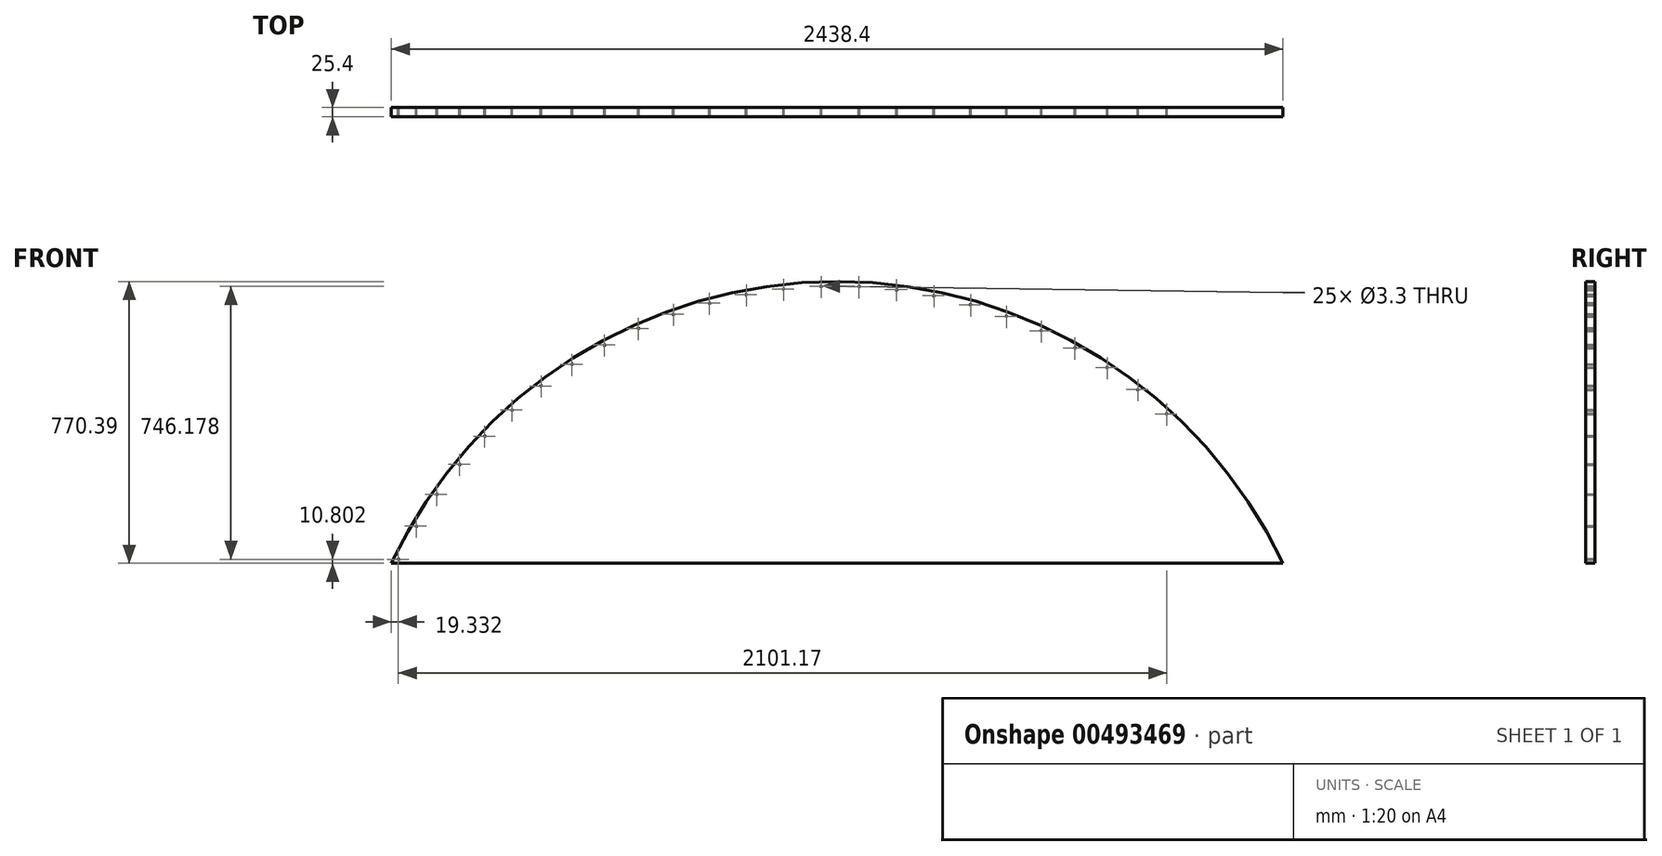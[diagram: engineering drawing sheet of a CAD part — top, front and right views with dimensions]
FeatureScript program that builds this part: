
annotation { "Feature Type Name" : "Feature", "Feature Type Description" : "" }
export const myFeature = defineFeature(function(context is Context, id is Id, definition is map)
    precondition{}
    {
        {
            var Q0;
            Q0=qCreatedBy(makeId("Front.planeOp"),FACE);
            var sketch = newSketch(context, id + "F0", { "sketchPlane" : qUnion([Q0])});
            skArc(sketch, "E0", {"start": v(1219.2, 0) * mm, "mid": v(0, 770.39) * mm, "end": v(-1219.2, 0) * mm});
            skLineSegment(sketch, "E1", {"start": v(-1219.2, 0) * mm, "end": v(1219.2, 0) * mm});
            skLineSegment(sketch, "E2", {"start": v(0, -579.55) * mm, "end": v(-923.4, 883.94) * mm, "construction": true});
            skLineSegment(sketch, "E3", {"start": v(0, -579.55) * mm, "end": v(0, 1034.52) * mm, "construction": true});
            skLineSegment(sketch, "E4", {"start": v(0, -579.55) * mm, "end": v(860.18, 783.76) * mm, "construction": true});
            skLineSegment(sketch, "E5", {"start": v(0, -579.55) * mm, "end": v(-1219.2, 0) * mm, "construction": true});
            skLineSegment(sketch, "E6", {"start": v(0, -579.55) * mm, "end": v(1219.2, 0) * mm, "construction": true});
            skArc(sketch, "E7.0", {"start": v(1196.26, -10.9) * mm, "mid": v(0, 744.99) * mm, "end": v(-1196.26, -10.9) * mm});
            skArc(sketch, "E8.0", {"start": v(1207.73, -5.45) * mm, "mid": v(0, 757.69) * mm, "end": v(-1207.73, -5.45) * mm, "construction": true});
            skPoint(sketch, "E9", {"position": v(-1199.87, 10.8) * mm});
            skPoint(sketch, "E10.1.0", {"position": v(-1150.75, 101.6) * mm});
            skPoint(sketch, "E10.2.0", {"position": v(-1094.78, 188.34) * mm});
            skPoint(sketch, "E10.3.0", {"position": v(-1032.29, 270.5) * mm});
            skPoint(sketch, "E10.4.0", {"position": v(-963.64, 347.6) * mm});
            skPoint(sketch, "E10.5.0", {"position": v(-889.25, 419.17) * mm});
            skPoint(sketch, "E10.6.0", {"position": v(-809.56, 484.79) * mm});
            skPoint(sketch, "E10.7.0", {"position": v(-725.05, 544.07) * mm});
            skPoint(sketch, "E10.8.0", {"position": v(-636.21, 596.65) * mm});
            skPoint(sketch, "E10.9.0", {"position": v(-543.58, 642.22) * mm});
            skPoint(sketch, "E10.10.0", {"position": v(-447.72, 680.51) * mm});
            skPoint(sketch, "E10.11.0", {"position": v(-349.19, 711.3) * mm});
            skPoint(sketch, "E10.12.0", {"position": v(-248.57, 734.38) * mm});
            skPoint(sketch, "E10.13.0", {"position": v(-146.47, 749.64) * mm});
            skPoint(sketch, "E10.14.0", {"position": v(-43.5, 756.98) * mm});
            skPoint(sketch, "E10.15.0", {"position": v(59.72, 756.35) * mm});
            skPoint(sketch, "E10.16.0", {"position": v(162.6, 747.77) * mm});
            skPoint(sketch, "E10.17.0", {"position": v(264.5, 731.27) * mm});
            skPoint(sketch, "E10.18.0", {"position": v(364.82, 706.96) * mm});
            skPoint(sketch, "E10.19.0", {"position": v(462.98, 674.99) * mm});
            skPoint(sketch, "E10.20.0", {"position": v(558.37, 635.53) * mm});
            skPoint(sketch, "E10.21.0", {"position": v(650.44, 588.84) * mm});
            skPoint(sketch, "E10.22.0", {"position": v(738.63, 535.19) * mm});
            skPoint(sketch, "E10.23.0", {"position": v(822.42, 474.89) * mm});
            skPoint(sketch, "E10.24.0", {"position": v(901.3, 408.3) * mm});
            skPoint(sketch, "E10.25.0", {"position": v(974.82, 335.84) * mm});
            skPoint(sketch, "E10.26.0", {"position": v(1042.53, 257.91) * mm});
            skPoint(sketch, "E10.27.0", {"position": v(1104.02, 175) * mm});
            skPoint(sketch, "E10.28.0", {"position": v(1158.94, 87.59) * mm});
            skPoint(sketch, "E10.29.0", {"position": v(1206.94, -3.8) * mm});
            skLineSegment(sketch, "E10.anchor1", {"start": v(0, -579.55) * mm, "end": v(-1199.87, 10.8) * mm, "construction": true});
            skLineSegment(sketch, "E10.anchor2", {"start": v(0, -579.55) * mm, "end": v(1206.94, -3.8) * mm, "construction": true});
            skSolve(sketch);
        }
        {
            var Q0;
            Q0 = qSketchRegion(id + "F0", true);
            extrude(context, id + "F1", {"entities" : qUnion([Q0]), "oppositeDirection" : true, "depth" : 25.4 * mm, "offsetDistance" : 25.4 * mm});
        }
        {
            var Q0;
            Q0=makeQuery(id+"F0.imprint","IMPRINT",FACE,{"disambiguationData":[TD([[makeQuery(id+"F0.imprint","IMPRINT",EDGE,{"derivedFrom":sQuery(id+"F0.wireOp",EDGE,"E0")}),1.0]])]});
            var sketch = newSketch(context, id + "F2", { "sketchPlane" : qUnion([Q0])});
            skLineSegment(sketch, "E11", {"start": v(-1385.99, 67.82) * mm, "end": v(1291.38, 67.82) * mm, "construction": true});
            skLineSegment(sketch, "E12.0", {"start": v(-1219.2, 0) * mm, "end": v(1219.2, 0) * mm});
            skSolve(sketch);
        }
        {
            var Q0;
            Q0=makeQuery(id+"F0.imprint","IMPRINT",FACE,{"disambiguationData":[TD([[makeQuery(id+"F0.imprint","IMPRINT",EDGE,{"derivedFrom":sQuery(id+"F0.wireOp",EDGE,"E0")}),1.0]])]});
            cPlane(context, id + "F3", {"entities" : qUnion([Q0]), "cplaneType" : CPlaneType.OFFSET, "offset" : 160.02 * mm, "width" : 152.4 * mm, "height" : 152.4 * mm});
        }
        {
            var Q0;
            Q0=qCreatedBy(id+"F3.planeOp",FACE);
            var sketch = newSketch(context, id + "F4", { "sketchPlane" : qUnion([Q0])});
            skLineSegment(sketch, "E13.0", {"start": v(-1385.99, 67.82) * mm, "end": v(1291.38, 67.82) * mm});
            skPoint(sketch, "E14.0", {"position": v(0, 0) * mm});
            skLineSegment(sketch, "E15.0", {"start": v(-1219.2, 0) * mm, "end": v(1219.2, 0) * mm});
            skLineSegment(sketch, "E16.bottom", {"start": v(-1219.2, 67.82) * mm, "end": v(1219.2, 67.82) * mm});
            skLineSegment(sketch, "E16.top", {"start": v(-1219.2, 372.62) * mm, "end": v(1219.2, 372.62) * mm});
            skLineSegment(sketch, "E16.left", {"start": v(-1219.2, 67.82) * mm, "end": v(-1219.2, 372.62) * mm});
            skLineSegment(sketch, "E16.right", {"start": v(1219.2, 67.82) * mm, "end": v(1219.2, 372.62) * mm});
            skSolve(sketch);
        }
        {
            var Q0;
            Q0=makeQuery(id+"F0YqCXG83JIjHPd_1.opExtrude","CAP_FACE",FACE,{"disambiguationData":[OSD([sQuery(id+"F4.wireOp",EDGE,"E16.bottom"),sQuery(id+"F4.wireOp",EDGE,"E16.top"),sQuery(id+"F4.wireOp",EDGE,"E16.left"),sQuery(id+"F4.wireOp",EDGE,"E16.right")])],"isStart":true});
            var sketch = newSketch(context, id + "F5", { "sketchPlane" : qUnion([Q0])});
            skLineSegment(sketch, "E17.0", {"start": v(0, -579.55) * mm, "end": v(923.4, 883.94) * mm});
            skLineSegment(sketch, "E18.0", {"start": v(0, -579.55) * mm, "end": v(0, 1034.52) * mm});
            skLineSegment(sketch, "E19.0", {"start": v(0, -579.55) * mm, "end": v(-860.18, 783.76) * mm});
            skLineSegment(sketch, "E20", {"start": v(-1219.2, 220.22) * mm, "end": v(1219.2, 220.22) * mm, "construction": true});
            skPoint(sketch, "E21", {"position": v(-504.61, 220.22) * mm});
            skPoint(sketch, "E22", {"position": v(504.61, 220.22) * mm});
            skSolve(sketch);
        }
        {
            var Q0;
            Q0=sQuery(id+"F0.wireOp",VERTEX,"E9");
            var Q1;
            Q1=sQuery(id+"F0.wireOp",VERTEX,"E10.1.0");
            var Q2;
            Q2=sQuery(id+"F0.wireOp",VERTEX,"E10.2.0");
            var Q3;
            Q3=sQuery(id+"F0.wireOp",VERTEX,"E10.3.0");
            var Q4;
            Q4=sQuery(id+"F0.wireOp",VERTEX,"E10.4.0");
            var Q5;
            Q5=sQuery(id+"F0.wireOp",VERTEX,"E10.5.0");
            var Q6;
            Q6=sQuery(id+"F0.wireOp",VERTEX,"E10.6.0");
            var Q7;
            Q7=sQuery(id+"F0.wireOp",VERTEX,"E10.7.0");
            var Q8;
            Q8=sQuery(id+"F0.wireOp",VERTEX,"E10.8.0");
            var Q9;
            Q9=sQuery(id+"F0.wireOp",VERTEX,"E10.9.0");
            var Q10;
            Q10=sQuery(id+"F0.wireOp",VERTEX,"E10.10.0");
            var Q11;
            Q11=sQuery(id+"F0.wireOp",VERTEX,"E10.11.0");
            var Q12;
            Q12=sQuery(id+"F0.wireOp",VERTEX,"E10.12.0");
            var Q13;
            Q13=sQuery(id+"F0.wireOp",VERTEX,"E10.13.0");
            var Q14;
            Q14=sQuery(id+"F0.wireOp",VERTEX,"E10.14.0");
            var Q15;
            Q15=sQuery(id+"F0.wireOp",VERTEX,"E10.15.0");
            var Q16;
            Q16=sQuery(id+"F0.wireOp",VERTEX,"E10.16.0");
            var Q17;
            Q17=sQuery(id+"F0.wireOp",VERTEX,"E10.17.0");
            var Q18;
            Q18=sQuery(id+"F0.wireOp",VERTEX,"E10.18.0");
            var Q19;
            Q19=sQuery(id+"F0.wireOp",VERTEX,"E10.19.0");
            var Q20;
            Q20=sQuery(id+"F0.wireOp",VERTEX,"E10.20.0");
            var Q21;
            Q21=sQuery(id+"F0.wireOp",VERTEX,"E10.21.0");
            var Q22;
            Q22=sQuery(id+"F0.wireOp",VERTEX,"E10.22.0");
            var Q23;
            Q23=sQuery(id+"F0.wireOp",VERTEX,"E10.23.0");
            var Q24;
            Q24=sQuery(id+"F0.wireOp",VERTEX,"E10.24.0");
            var Q25;
            Q25=makeQuery(id+"F1.opExtrude","SWEPT_BODY",BODY,{"disambiguationData":[OSD([sQuery(id+"F0.wireOp",EDGE,"E0"),sQuery(id+"F0.wireOp",EDGE,"E1")])]});
            hole(context, id + "F6", {"style" : HoleStyle.SIMPLE, "endStyle" : HoleEndStyle.THROUGH, "standardTappedOrClearance" : lookupTablePath({ "fit" : "Normal", "standard" : "ISO", "size" : "M3", "type" : "Clearance" }), "standardBlindInLast" : lookupTablePath({ "fit" : "Standard", "standard" : "ISO", "size" : "M3", "type" : "Clearance" }), "holeDiameter" : 3.3 * mm, "majorDiameter" : 6.35 * mm, "isTappedThrough" : true, "tappedDepth" : 12.7 * mm, "tapClearance" : 3, "startFromSketch" : true, "locations" : qUnion([Q0, Q1, Q2, Q3, Q4, Q5, Q6, Q7, Q8, Q9, Q10, Q11, Q12, Q13, Q14, Q15, Q16, Q17, Q18, Q19, Q20, Q21, Q22, Q23, Q24]), "scope" : qUnion([Q25])});
        }
    });
